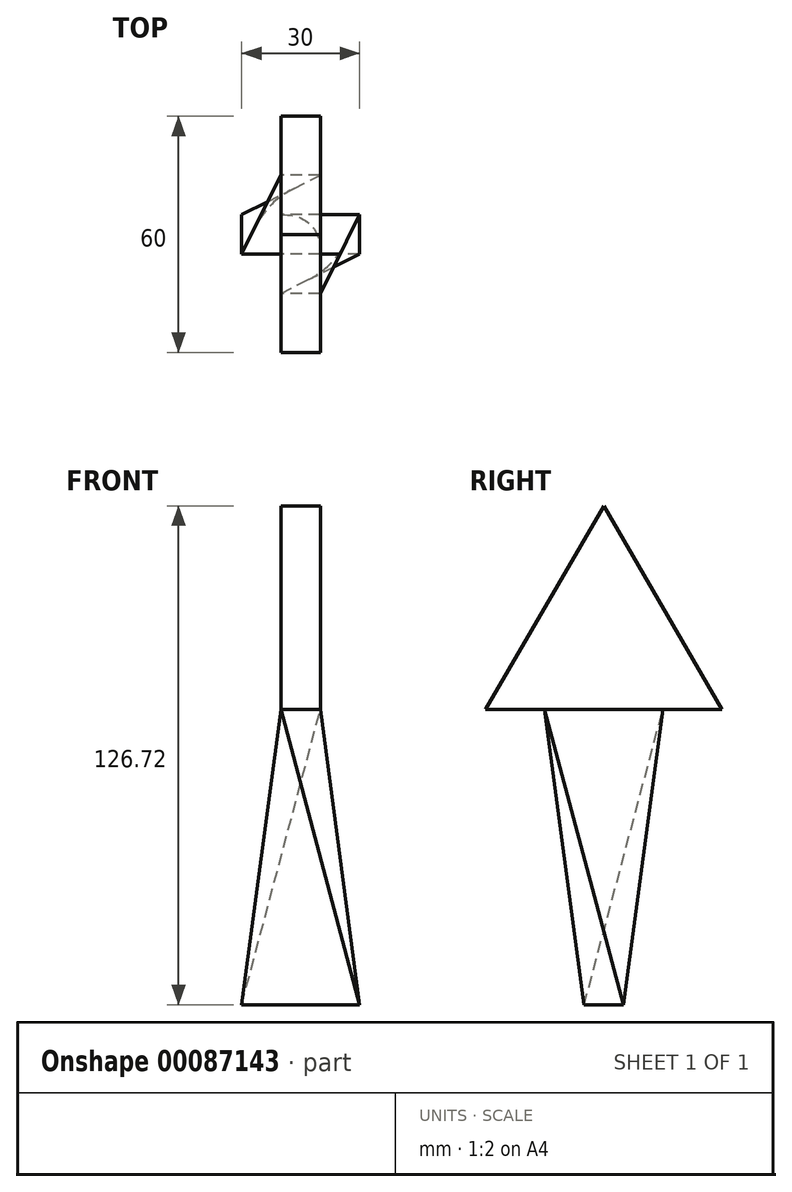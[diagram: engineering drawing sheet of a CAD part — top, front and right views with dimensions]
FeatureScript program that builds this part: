
annotation { "Feature Type Name" : "Feature", "Feature Type Description" : "" }
export const myFeature = defineFeature(function(context is Context, id is Id, definition is map)
    precondition{}
    {
        {
            var Q0;
            Q0=qCreatedBy(makeId("Top.planeOp"),FACE);
            cPlane(context, id + "F0", {"entities" : qUnion([Q0]), "cplaneType" : CPlaneType.OFFSET, "offset" : 75 * mm, "width" : 150 * mm, "height" : 150 * mm});
        }
        {
            var Q0;
            Q0=qCreatedBy(makeId("Top.planeOp"),FACE);
            var sketch = newSketch(context, id + "F1", { "sketchPlane" : qUnion([Q0])});
            skLineSegment(sketch, "E0.bottom", {"start": v(15, -5) * mm, "end": v(-15, -5) * mm});
            skLineSegment(sketch, "E0.top", {"start": v(15, 5) * mm, "end": v(-15, 5) * mm});
            skLineSegment(sketch, "E0.left", {"start": v(15, -5) * mm, "end": v(15, 5) * mm});
            skLineSegment(sketch, "E0.right", {"start": v(-15, -5) * mm, "end": v(-15, 5) * mm});
            skPoint(sketch, "E0.middle", {"position": v(0, 0) * mm});
            skSolve(sketch);
        }
        {
            var Q0;
            Q0=qCreatedBy(id+"F0.planeOp",FACE);
            var sketch = newSketch(context, id + "F2", { "sketchPlane" : qUnion([Q0])});
            skLineSegment(sketch, "E1.bottom", {"start": v(5, 15) * mm, "end": v(-5, 15) * mm});
            skLineSegment(sketch, "E1.top", {"start": v(5, -15) * mm, "end": v(-5, -15) * mm});
            skLineSegment(sketch, "E1.left", {"start": v(5, 15) * mm, "end": v(5, -15) * mm});
            skLineSegment(sketch, "E1.right", {"start": v(-5, 15) * mm, "end": v(-5, -15) * mm});
            skPoint(sketch, "E1.middle", {"position": v(0, 0) * mm});
            skSolve(sketch);
        }
        {
            var Q0;
            Q0=sQuery(id+"F2.wireOp",EDGE,"E1.top");
            var Q1;
            Q1=sQuery(id+"F1.wireOp",EDGE,"E0.bottom");
            cPlane(context, id + "F3", {"entities" : qUnion([Q0, Q1]), "cplaneType" : CPlaneType.LINE_ANGLE, "offset" : 150 * mm, "angle" : 0 * degree, "width" : 150 * mm, "height" : 150 * mm});
        }
        {
            var Q0;
            Q0=qCreatedBy(id+"F3.planeOp",FACE);
            var sketch = newSketch(context, id + "F4", { "sketchPlane" : qUnion([Q0])});
            skLineSegment(sketch, "E2", {"start": v(-5, 76.32) * mm, "end": v(15, 0.66) * mm});
            skSolve(sketch);
        }
        {
            var Q0;
            Q0=sQuery(id+"F1.wireOp",EDGE,"E0.right");
            var Q1;
            Q1=sQuery(id+"F2.wireOp",EDGE,"E1.right");
            cPlane(context, id + "F5", {"entities" : qUnion([Q0, Q1]), "cplaneType" : CPlaneType.LINE_ANGLE, "offset" : 150 * mm, "angle" : 0 * degree, "width" : 150 * mm, "height" : 150 * mm});
        }
        {
            var Q0;
            Q0=qCreatedBy(id+"F5.planeOp",FACE);
            var sketch = newSketch(context, id + "F6", { "sketchPlane" : qUnion([Q0])});
            skLineSegment(sketch, "E3", {"start": v(-5, -1.98) * mm, "end": v(15, 73.68) * mm});
            skSolve(sketch);
        }
        {
            var Q0;
            Q0=sQuery(id+"F2.wireOp",EDGE,"E1.bottom");
            var Q1;
            Q1=sQuery(id+"F1.wireOp",EDGE,"E0.top");
            cPlane(context, id + "F7", {"entities" : qUnion([Q0, Q1]), "cplaneType" : CPlaneType.LINE_ANGLE, "offset" : 150 * mm, "angle" : 0 * degree, "width" : 150 * mm, "height" : 150 * mm});
        }
        {
            var Q0;
            Q0=qCreatedBy(id+"F7.planeOp",FACE);
            var sketch = newSketch(context, id + "F8", { "sketchPlane" : qUnion([Q0])});
            skLineSegment(sketch, "E4", {"start": v(-15, 0.66) * mm, "end": v(5, 76.32) * mm});
            skSolve(sketch);
        }
        {
            var Q0;
            Q0=sQuery(id+"F2.wireOp",EDGE,"E1.left");
            var Q1;
            Q1=sQuery(id+"F1.wireOp",EDGE,"E0.left");
            cPlane(context, id + "F9", {"entities" : qUnion([Q0, Q1]), "cplaneType" : CPlaneType.LINE_ANGLE, "offset" : 150 * mm, "angle" : 0 * degree, "width" : 150 * mm, "height" : 150 * mm});
        }
        {
            var Q0;
            Q0=qCreatedBy(id+"F9.planeOp",FACE);
            var sketch = newSketch(context, id + "F10", { "sketchPlane" : qUnion([Q0])});
            skLineSegment(sketch, "E5", {"start": v(-15, 73.68) * mm, "end": v(5, -1.98) * mm});
            skSolve(sketch);
        }
        {
            var Q0;
            Q0=makeQuery(id+"F2.imprint","IMPRINT",FACE,{"disambiguationData":[TD([[makeQuery(id+"F2.imprint","IMPRINT",EDGE,{"derivedFrom":sQuery(id+"F2.wireOp",EDGE,"E1.bottom")}),1.0]])]});
            var Q1;
            Q1=makeQuery(id+"F1.imprint","IMPRINT",FACE,{"disambiguationData":[TD([[makeQuery(id+"F1.imprint","IMPRINT",EDGE,{"derivedFrom":sQuery(id+"F1.wireOp",EDGE,"E0.bottom")}),-1.0]])]});
            var Q2;
            Q2=sQuery(id+"F10.wireOp",EDGE,"E5");
            var Q3;
            Q3=sQuery(id+"F4.wireOp",EDGE,"E2");
            var Q4;
            Q4=sQuery(id+"F6.wireOp",EDGE,"E3");
            var Q5;
            Q5=sQuery(id+"F8.wireOp",EDGE,"E4");
            loft(context, id + "F11", {"addGuides" : true, "sheetProfilesArray" : [{ "sheetProfileEntities" : qUnion([Q0]) }, { "sheetProfileEntities" : qUnion([Q1]) }], "guidesArray" : [{ "guideEntities" : qUnion([Q2]), "guideDerivativeType" : LoftGuideDerivativeType.DEFAULT, "guideDerivativeMagnitude" : 1 }, { "guideEntities" : qUnion([Q3]), "guideDerivativeType" : LoftGuideDerivativeType.DEFAULT, "guideDerivativeMagnitude" : 1 }, { "guideEntities" : qUnion([Q4]), "guideDerivativeType" : LoftGuideDerivativeType.DEFAULT, "guideDerivativeMagnitude" : 1 }, { "guideEntities" : qUnion([Q5]), "guideDerivativeType" : LoftGuideDerivativeType.DEFAULT, "guideDerivativeMagnitude" : 1 }]});
        }
        {
            var Q0;
            Q0=makeQuery(id+"F11.opLoft","CAP_FACE",FACE,{"disambiguationData":[OSD([makeQuery(id+"F2.imprint","IMPRINT",FACE,{"disambiguationData":[TD([[makeQuery(id+"F2.imprint","IMPRINT",EDGE,{"derivedFrom":sQuery(id+"F2.wireOp",EDGE,"E1.bottom")}),1.0]])]})])],"isStart":true});
            var sketch = newSketch(context, id + "F12", { "sketchPlane" : qUnion([Q0])});
            skLineSegment(sketch, "E6.0", {"start": v(-5, -15) * mm, "end": v(-5, 15) * mm});
            skLineSegment(sketch, "E6.1", {"start": v(5, -15) * mm, "end": v(-5, -15) * mm});
            skLineSegment(sketch, "E6.2", {"start": v(5, 15) * mm, "end": v(5, -15) * mm});
            skLineSegment(sketch, "E6.3", {"start": v(-5, 15) * mm, "end": v(5, 15) * mm});
            skLineSegment(sketch, "E7.0", {"start": v(-5, 30) * mm, "end": v(5, 30) * mm});
            skLineSegment(sketch, "E8.0", {"start": v(5, -30) * mm, "end": v(-5, -30) * mm});
            skLineSegment(sketch, "E9", {"start": v(-5, 15) * mm, "end": v(-5, 30) * mm});
            skLineSegment(sketch, "E10", {"start": v(-5, -15) * mm, "end": v(-5, -30) * mm});
            skLineSegment(sketch, "E11", {"start": v(5, -30) * mm, "end": v(5, -15) * mm});
            skLineSegment(sketch, "E12", {"start": v(5, 30) * mm, "end": v(5, 15) * mm});
            skSolve(sketch);
        }
        {
            var Q0;
            Q0 = qSketchRegion(id + "F12", true);
            extrude(context, id + "F13", {"entities" : qUnion([Q0]), "operationType" : NewBodyOperationType.ADD, "depth" : 51.72 * mm});
        }
        {
            var Q0;
            Q0=makeQuery(id+"F13.opExtrude","SWEPT_FACE",FACE,{"disambiguationData":[OSD([sQuery(id+"F12.wireOp",EDGE,"E6.0"),sQuery(id+"F12.wireOp",EDGE,"E9"),sQuery(id+"F12.wireOp",EDGE,"E10")])]});
            var sketch = newSketch(context, id + "F14", { "sketchPlane" : qUnion([Q0])});
            skLineSegment(sketch, "E13", {"start": v(-30, 75) * mm, "end": v(0, 126.72) * mm});
            skLineSegment(sketch, "E14", {"start": v(0, 126.72) * mm, "end": v(30, 75) * mm});
            skLineSegment(sketch, "E15", {"start": v(30, 75) * mm, "end": v(37.35, 75) * mm});
            skLineSegment(sketch, "E16", {"start": v(37.35, 75) * mm, "end": v(37.35, 133.38) * mm});
            skLineSegment(sketch, "E17", {"start": v(37.35, 133.38) * mm, "end": v(-35.26, 134.83) * mm});
            skLineSegment(sketch, "E18", {"start": v(-35.26, 134.83) * mm, "end": v(-35.26, 75) * mm});
            skLineSegment(sketch, "E19", {"start": v(-35.26, 75) * mm, "end": v(-30, 75) * mm});
            skSolve(sketch);
        }
        {
            var Q0;
            Q0 = qSketchRegion(id + "F14", true);
            extrude(context, id + "F15", {"entities" : qUnion([Q0]), "operationType" : NewBodyOperationType.REMOVE, "oppositeDirection" : true, "depth" : 25 * mm});
        }
    });
